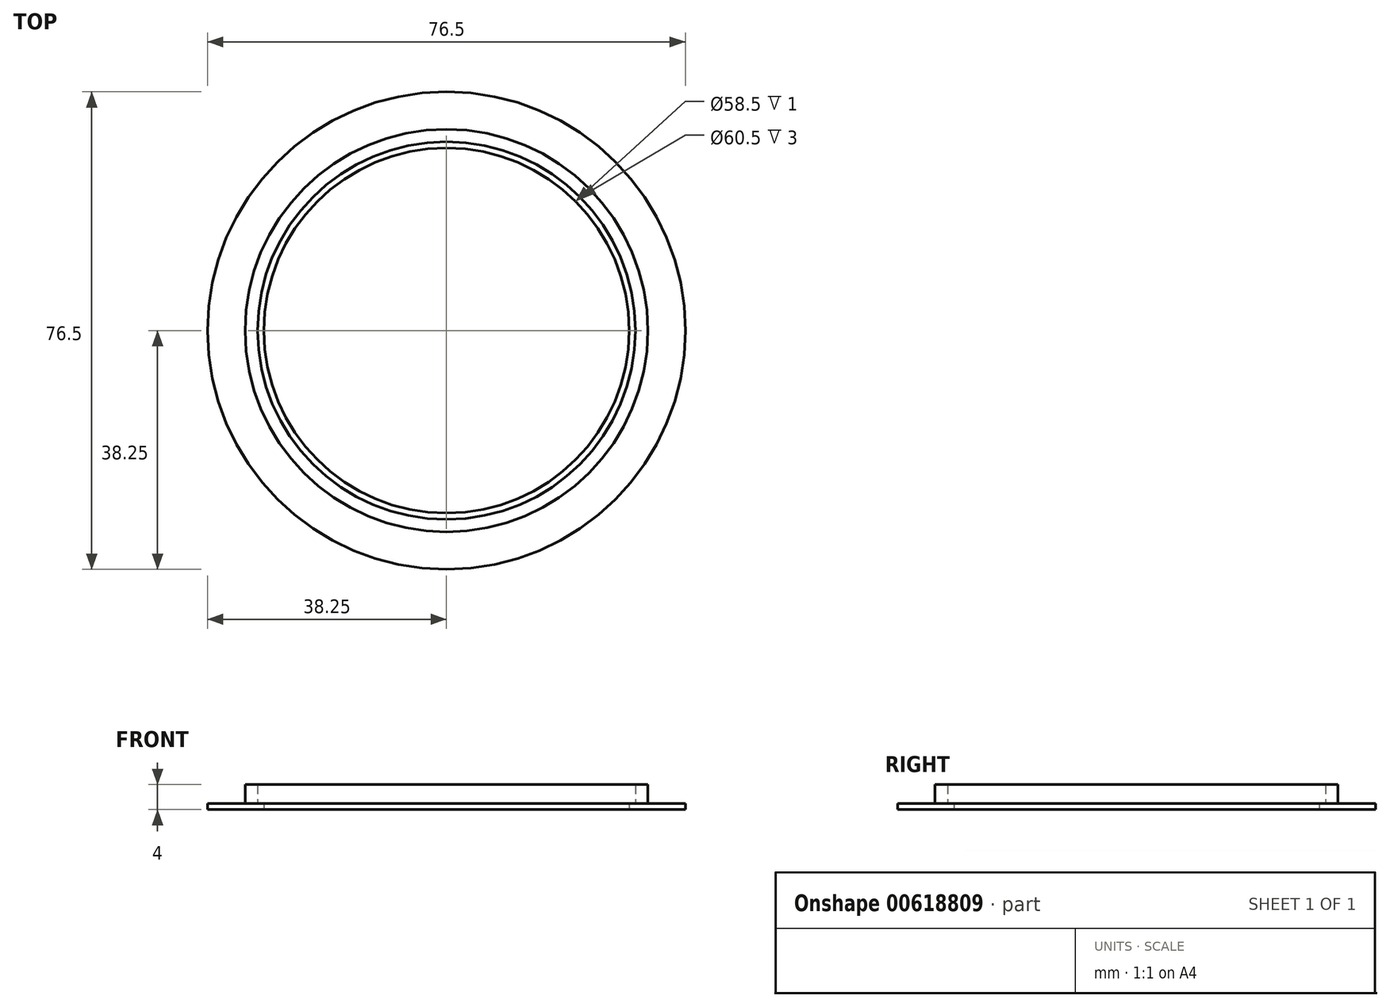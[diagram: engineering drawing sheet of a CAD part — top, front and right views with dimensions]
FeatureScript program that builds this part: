
annotation { "Feature Type Name" : "Feature", "Feature Type Description" : "" }
export const myFeature = defineFeature(function(context is Context, id is Id, definition is map)
    precondition{}
    {
        {
            var Q0;
            Q0=qCreatedBy(makeId("Top.planeOp"),FACE);
            var sketch = newSketch(context, id + "F0", { "sketchPlane" : qUnion([Q0])});
            skCircle(sketch, "E0", {"center": v(0, 0) * mm, "radius": 29.25 * mm});
            skCircle(sketch, "E1", {"center": v(0, 0) * mm, "radius": 38.25 * mm});
            skPoint(sketch, "E2", {"position": v(0, 29.25) * mm});
            skPoint(sketch, "E3", {"position": v(0, 38.25) * mm});
            skSolve(sketch);
        }
        {
            var Q0;
            Q0 = qSketchRegion(id + "F0", true);
            extrude(context, id + "F1", {"entities" : qUnion([Q0]), "depth" : 1 * mm, "offsetDistance" : 25 * mm});
        }
        {
            var Q0;
            Q0=makeQuery(id+"F1.opExtrude","CAP_FACE",FACE,{"disambiguationData":[OSD([sQuery(id+"F0.wireOp",EDGE,"E0"),sQuery(id+"F0.wireOp",EDGE,"E1")])],"isStart":false});
            var sketch = newSketch(context, id + "F2", { "sketchPlane" : qUnion([Q0])});
            skCircle(sketch, "E4", {"center": v(0, 0) * mm, "radius": 30.25 * mm});
            skCircle(sketch, "E5", {"center": v(0, 0) * mm, "radius": 32.25 * mm});
            skPoint(sketch, "E6", {"position": v(0, 30.25) * mm});
            skPoint(sketch, "E7", {"position": v(0, 32.25) * mm});
            skSolve(sketch);
        }
        {
            var Q0;
            Q0 = qSketchRegion(id + "F2", true);
            extrude(context, id + "F3", {"entities" : qUnion([Q0]), "operationType" : NewBodyOperationType.ADD, "depth" : 3 * mm, "offsetDistance" : 25 * mm});
        }
    });
